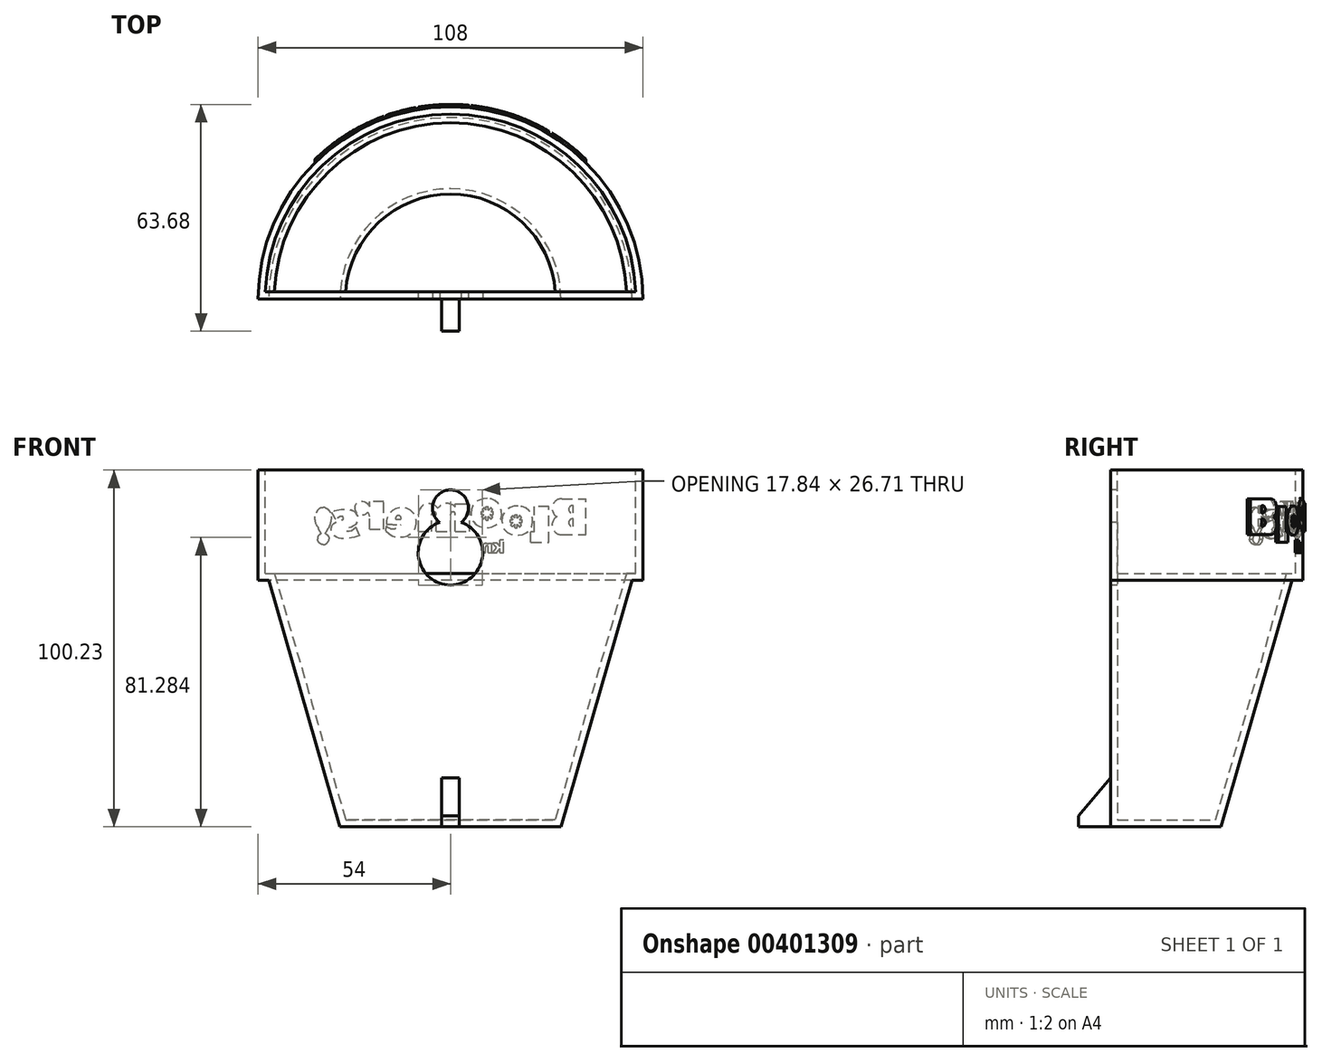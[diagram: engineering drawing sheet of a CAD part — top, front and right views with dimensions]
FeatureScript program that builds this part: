
annotation { "Feature Type Name" : "Feature", "Feature Type Description" : "" }
export const myFeature = defineFeature(function(context is Context, id is Id, definition is map)
    precondition{}
    {
        {
            var Q0;
            Q0=qCreatedBy(makeId("Front.planeOp"),FACE);
            var sketch = newSketch(context, id + "F0", { "sketchPlane" : qUnion([Q0])});
            skLineSegment(sketch, "E0", {"start": v(0, 49.42) * mm, "end": v(-54, 49.42) * mm});
            skLineSegment(sketch, "E1", {"start": v(-54, 49.42) * mm, "end": v(-54, 18.42) * mm});
            skLineSegment(sketch, "E2", {"start": v(0, -50.8) * mm, "end": v(-31, -50.8) * mm});
            skLineSegment(sketch, "E3", {"start": v(-54, 18.42) * mm, "end": v(-51, 18.42) * mm});
            skLineSegment(sketch, "E4", {"start": v(0, 49.42) * mm, "end": v(0, -50.8) * mm});
            skLineSegment(sketch, "E5", {"start": v(-51, 18.42) * mm, "end": v(-31, -50.8) * mm});
            skLineSegment(sketch, "E6.MirrorCS", {"start": v(0, 49.42) * mm, "end": v(54, 49.42) * mm});
            skLineSegment(sketch, "E7.MirrorCS", {"start": v(54, 49.42) * mm, "end": v(54, 18.42) * mm});
            skLineSegment(sketch, "E8.MirrorCS", {"start": v(54, 18.42) * mm, "end": v(51, 18.42) * mm});
            skLineSegment(sketch, "E9.MirrorCS", {"start": v(51, 18.42) * mm, "end": v(31, -50.8) * mm});
            skLineSegment(sketch, "E10.MirrorCS", {"start": v(0, -50.8) * mm, "end": v(31, -50.8) * mm});
            skSolve(sketch);
        }
        {
            var Q0;
            {var subQ0=sQuery(id+"F0.wireOp",EDGE,"E3");Q0=makeQuery(id+"F0.imprint","IMPRINT",FACE,{"disambiguationData":[TD([[makeQuery(id+"F0.imprint","IMPRINT",EDGE,{"derivedFrom":subQ0}),1.0]])]});}
            var Q1;
            {var subQ1=sQuery(id+"F0.wireOp",EDGE,"E0");Q1=makeQuery(id+"F0.imprint","IMPRINT",FACE,{"disambiguationData":[TD([[makeQuery(id+"F0.imprint","IMPRINT",EDGE,{"derivedFrom":subQ1}),1.0]])]});}
            var Q2;
            Q2=makeQuery(id+"F0.imprint","IMPRINT",FACE,{"disambiguationData":[TD([[makeQuery(id+"F0.imprint","IMPRINT",EDGE,{"derivedFrom":sQuery(id+"F0.wireOp",EDGE,"Kfnrekvc-ZjTY-c2iQ-cK4z-hKnBe4uEAVNk")}),1.0]])]});
            var Q3;
            Q3=sQuery(id+"F0.wireOp",EDGE,"E4");
            revolve(context, id + "F1", {"entities" : qUnion([Q0, Q1, Q2]), "axis" : qUnion([Q3]), "revolveType" : RevolveType.ONE_DIRECTION, "angle" : 180 * degree});
        }
        {
            var Q0;
            Q0=makeQuery(id+"FK2OT3XlAi37Aaq_1.splitOp","SPLIT",FACE,{"derivedFrom":makeQuery(id+"F1.opRevolve","SWEPT_FACE",FACE,{"disambiguationData":[OSD([sQuery(id+"F0.wireOp",EDGE,"E0")])]}),"isFromBackBody":true});
            shell(context, id + "F2", {"entities" : qUnion([Q0]), "thickness" : 2 * mm});
        }
        {
            var Q0;
            Q0=qCreatedBy(makeId("Front.planeOp"),FACE);
            var sketch = newSketch(context, id + "F3", { "sketchPlane" : qUnion([Q0])});
            skLineSegment(sketch, "E11.bottom", {"start": v(-2.5, -35.8) * mm, "end": v(2.5, -35.8) * mm});
            skLineSegment(sketch, "E11.top", {"start": v(-2.5, -50.8) * mm, "end": v(2.5, -50.8) * mm});
            skLineSegment(sketch, "E11.left", {"start": v(-2.5, -35.8) * mm, "end": v(-2.5, -50.8) * mm});
            skLineSegment(sketch, "E11.right", {"start": v(2.5, -35.8) * mm, "end": v(2.5, -50.8) * mm});
            skPoint(sketch, "E11.middle", {"position": v(0, -43.3) * mm});
            skSolve(sketch);
        }
        {
            var Q0;
            Q0=qSketchRegion(id+"F3",true);
            extrude(context, id + "F4", {"entities" : qUnion([Q0]), "operationType" : NewBodyOperationType.ADD, "depth" : 9 * mm});
        }
        {
            var Q0;
            Q0=qCreatedBy(makeId("Front.planeOp"),FACE);
            var sketch = newSketch(context, id + "F5", { "sketchPlane" : qUnion([Q0])});
            skCircle(sketch, "E12", {"center": v(0, 38.78) * mm, "radius": 5.05 * mm});
            skCircle(sketch, "E13", {"center": v(0, 26.17) * mm, "radius": 9.05 * mm});
            skSolve(sketch);
        }
        {
            var Q0;
            {var subQ0=sQuery(id+"F5.wireOp",EDGE,"E13");var subQ1=sQuery(id+"F5.wireOp",EDGE,"E12");var subQ2=makeQuery(id+"F5.imprint","INTERSECT",VERTEX,{"disambiguationData":[OD(0.0)],"derivedFrom":[subQ1,subQ0]});Q0=makeQuery(id+"F5.imprint","IMPRINT",FACE,{"disambiguationData":[TD([[makeQuery(id+"F5.imprint","IMPRINT",EDGE,{"disambiguationData":[TD([[subQ2,1.0]])],"derivedFrom":subQ1}),1.0]])]});}
            var Q1;
            {var subQ0=sQuery(id+"F5.wireOp",EDGE,"E13");var subQ1=sQuery(id+"F5.wireOp",EDGE,"E12");var subQ2=makeQuery(id+"F5.imprint","INTERSECT",VERTEX,{"disambiguationData":[OD(0.0)],"derivedFrom":[subQ1,subQ0]});Q1=makeQuery(id+"F5.imprint","IMPRINT",FACE,{"disambiguationData":[TD([[makeQuery(id+"F5.imprint","IMPRINT",EDGE,{"disambiguationData":[TD([[subQ2,-1.0]])],"derivedFrom":subQ1}),-1.0]])]});}
            var Q2;
            {var subQ0=sQuery(id+"F5.wireOp",EDGE,"E13");var subQ1=sQuery(id+"F5.wireOp",EDGE,"E12");var subQ2=makeQuery(id+"F5.imprint","INTERSECT",VERTEX,{"disambiguationData":[OD(0.0)],"derivedFrom":[subQ1,subQ0]});Q2=makeQuery(id+"F5.imprint","IMPRINT",FACE,{"disambiguationData":[TD([[makeQuery(id+"F5.imprint","IMPRINT",EDGE,{"disambiguationData":[TD([[subQ2,-1.0]])],"derivedFrom":subQ1}),1.0]])]});}
            var Q3;
            Q3=sQuery(id+"F5.wireOp",EDGE,"E12");
            var Q4;
            Q4=sQuery(id+"F5.wireOp",EDGE,"E13");
            extrude(context, id + "F6", {"entities" : qUnion([Q0, Q1, Q2]), "operationType" : NewBodyOperationType.REMOVE, "surfaceEntities" : qUnion([Q3, Q4]), "oppositeDirection" : true, "depth" : 10 * mm});
        }
        {
            var Q0;
            Q0=makeQuery(id+"F4.opExtrude","CAP_EDGE",EDGE,{"disambiguationData":[OSD([sQuery(id+"F3.wireOp",EDGE,"E11.bottom")])],"isStart":false});
            chamfer(context, id + "F7", {"entities" : qUnion([Q0]), "chamferType" : ChamferType.OFFSET_ANGLE, "width" : 10 * mm, "oppositeDirection" : false, "angle" : 50 * degree, "tangentPropagation" : true});
        }
        {
            var Q0;
            Q0=makeQuery(id+"F2.opShell","OFFSET_FACE",FACE,{"disambiguationData":[OSD([sQuery(id+"F0.wireOp",EDGE,"E0"),sQuery(id+"F0.wireOp",EDGE,"E1"),sQuery(id+"F0.wireOp",EDGE,"E2"),sQuery(id+"F0.wireOp",EDGE,"E3"),sQuery(id+"F0.wireOp",EDGE,"E4"),sQuery(id+"F0.wireOp",EDGE,"E5")])]});
            cPlane(context, id + "F8", {"entities" : qUnion([Q0]), "cplaneType" : CPlaneType.OFFSET, "offset" : 52.7 * mm, "width" : 150 * mm, "height" : 150 * mm});
        }
        {
            var Q0;
            Q0=qCreatedBy(id+"F8.planeOp",FACE);
            var sketch = newSketch(context, id + "F9", { "sketchPlane" : qUnion([Q0])});
            skLineSegment(sketch, "E14", {"start": v(-37.98, 41.35) * mm, "end": v(-37.98, 31.23) * mm});
            skLineSegment(sketch, "E15", {"start": v(-37.98, 31.23) * mm, "end": v(-31.26, 31.23) * mm});
            skLineSegment(sketch, "E16", {"start": v(-37.98, 41.35) * mm, "end": v(-31.26, 41.35) * mm});
            skArc(sketch, "E17", {"start": v(-29.86, 36.3) * mm, "mid": v(-28.64, 39.36) * mm, "end": v(-31.26, 41.35) * mm});
            skArc(sketch, "E18", {"start": v(-31.26, 31.23) * mm, "mid": v(-28.62, 33.24) * mm, "end": v(-29.86, 36.3) * mm});
            skLineSegment(sketch, "E19", {"start": v(-34.46, 39.42) * mm, "end": v(-34.46, 37.35) * mm});
            skArc(sketch, "E20", {"start": v(-34.46, 37.35) * mm, "mid": v(-33.23, 38.38) * mm, "end": v(-34.46, 39.42) * mm});
            skArc(sketch, "E21", {"start": v(-34.46, 33.62) * mm, "mid": v(-33.23, 34.66) * mm, "end": v(-34.46, 35.69) * mm});
            skLineSegment(sketch, "E22.trimOffspring", {"start": v(-34.46, 35.69) * mm, "end": v(-34.46, 33.62) * mm});
            skLineSegment(sketch, "E23", {"start": v(-27.67, 39.2) * mm, "end": v(-27.67, 29.07) * mm});
            skLineSegment(sketch, "E24", {"start": v(-27.67, 29.07) * mm, "end": v(-22.58, 29.07) * mm});
            skLineSegment(sketch, "E25", {"start": v(-22.58, 29.07) * mm, "end": v(-22.58, 32.1) * mm});
            skLineSegment(sketch, "E26", {"start": v(-22.58, 32.1) * mm, "end": v(-23.6, 32.1) * mm});
            skLineSegment(sketch, "E27", {"start": v(-23.6, 32.1) * mm, "end": v(-23.6, 39.2) * mm});
            skLineSegment(sketch, "E28", {"start": v(-23.6, 39.2) * mm, "end": v(-27.67, 39.2) * mm});
            skFitSpline(sketch, "E29", {"points": [v(-18.97, 39.3) * mm, v(-20.87, 38.92) * mm, v(-22.46, 37.44) * mm, v(-22.99, 35.82) * mm, v(-22.97, 34.09) * mm, v(-22.03, 32.34) * mm, v(-20.21, 31.27) * mm, v(-18.57, 31.14) * mm, v(-16.6, 31.5) * mm, v(-14.9, 33.15) * mm, v(-14.42, 35.37) * mm, v(-14.96, 37.3) * mm, v(-16.45, 38.75) * mm, v(-18.2, 39.28) * mm, v(-18.97, 39.3) * mm]});
            skLineSegment(sketch, "E30.bottom", {"start": v(-18.74, 36.9) * mm, "end": v(-18.06, 36.9) * mm});
            skLineSegment(sketch, "E30.top", {"start": v(-18.74, 33.18) * mm, "end": v(-18.06, 33.18) * mm});
            skLineSegment(sketch, "E30.left", {"start": v(-18.74, 36.9) * mm, "end": v(-18.74, 35.88) * mm});
            skLineSegment(sketch, "E30.right", {"start": v(-18.06, 36.9) * mm, "end": v(-18.06, 35.97) * mm});
            skLineSegment(sketch, "E31.bottom", {"start": v(-20.12, 35.52) * mm, "end": v(-19.41, 35.52) * mm});
            skLineSegment(sketch, "E31.top", {"start": v(-20.12, 34.7) * mm, "end": v(-19.25, 34.7) * mm});
            skLineSegment(sketch, "E31.left", {"start": v(-20.12, 35.52) * mm, "end": v(-20.12, 34.7) * mm});
            skLineSegment(sketch, "E31.right", {"start": v(-16.76, 35.52) * mm, "end": v(-16.76, 34.7) * mm});
            skLineSegment(sketch, "E32", {"start": v(-19.97, 36.08) * mm, "end": v(-19.41, 35.52) * mm});
            skLineSegment(sketch, "E33", {"start": v(-17.4, 33.5) * mm, "end": v(-16.88, 34.02) * mm});
            skLineSegment(sketch, "E34", {"start": v(-19.45, 36.58) * mm, "end": v(-19.97, 36.08) * mm});
            skLineSegment(sketch, "E35", {"start": v(-19.97, 33.94) * mm, "end": v(-19.45, 33.42) * mm});
            skLineSegment(sketch, "E36", {"start": v(-19.45, 33.42) * mm, "end": v(-18.74, 34.17) * mm});
            skLineSegment(sketch, "E37", {"start": v(-16.94, 36.08) * mm, "end": v(-17.48, 36.58) * mm});
            skLineSegment(sketch, "E38", {"start": v(-17.48, 36.58) * mm, "end": v(-18.06, 35.97) * mm});
            skLineSegment(sketch, "E39.trimOffspring", {"start": v(-18.74, 35.88) * mm, "end": v(-19.45, 36.58) * mm});
            skLineSegment(sketch, "E40.trimOffspring", {"start": v(-19.25, 34.7) * mm, "end": v(-19.97, 33.94) * mm});
            skLineSegment(sketch, "E41.trimOffspring", {"start": v(-18.06, 34.17) * mm, "end": v(-17.4, 33.5) * mm});
            skLineSegment(sketch, "E42.trimOffspring", {"start": v(-18.74, 34.17) * mm, "end": v(-18.74, 33.18) * mm});
            skLineSegment(sketch, "E43.trimOffspring", {"start": v(-18.06, 34.17) * mm, "end": v(-18.06, 33.18) * mm});
            skLineSegment(sketch, "E44.trimOffspring", {"start": v(-17.47, 35.52) * mm, "end": v(-16.94, 36.08) * mm});
            skLineSegment(sketch, "E45.trimOffspring", {"start": v(-17.47, 35.52) * mm, "end": v(-16.76, 35.52) * mm});
            skLineSegment(sketch, "E46.trimOffspring", {"start": v(-17.56, 34.7) * mm, "end": v(-16.76, 34.7) * mm});
            skFitSpline(sketch, "E47", {"points": [v(-10.3, 41.42) * mm, v(-12.2, 41.04) * mm, v(-13.79, 39.56) * mm, v(-14.32, 37.94) * mm, v(-14.3, 36.2) * mm, v(-13.36, 34.46) * mm, v(-11.55, 33.39) * mm, v(-9.9, 33.26) * mm, v(-7.94, 33.62) * mm, v(-6.23, 35.27) * mm, v(-5.76, 37.49) * mm, v(-6.3, 39.41) * mm, v(-7.79, 40.86) * mm, v(-9.54, 41.4) * mm, v(-10.3, 41.42) * mm]});
            skLineSegment(sketch, "E48", {"start": v(-17.56, 34.7) * mm, "end": v(-16.88, 34.02) * mm});
            skLineSegment(sketch, "E49", {"start": v(-5.38, 32.17) * mm, "end": v(-5.38, 39.97) * mm});
            skLineSegment(sketch, "E50", {"start": v(-5.38, 39.97) * mm, "end": v(-1.39, 39.97) * mm});
            skLineSegment(sketch, "E51", {"start": v(-1.39, 39.97) * mm, "end": v(-1.39, 39) * mm});
            skLineSegment(sketch, "E52", {"start": v(-5.38, 32.17) * mm, "end": v(-1.38, 32.17) * mm});
            skLineSegment(sketch, "E53", {"start": v(-1.38, 32.17) * mm, "end": v(-1.38, 36.98) * mm});
            skLineSegment(sketch, "E54", {"start": v(0, 36.98) * mm, "end": v(0, 32.17) * mm});
            skLineSegment(sketch, "E55", {"start": v(0, 32.17) * mm, "end": v(3.95, 32.17) * mm});
            skLineSegment(sketch, "E56", {"start": v(3.95, 32.17) * mm, "end": v(3.95, 36.98) * mm});
            skLineSegment(sketch, "E57", {"start": v(5.25, 36.98) * mm, "end": v(5.25, 32.17) * mm});
            skLineSegment(sketch, "E58", {"start": v(5.25, 32.17) * mm, "end": v(9.02, 32.17) * mm});
            skLineSegment(sketch, "E59", {"start": v(9.02, 32.17) * mm, "end": v(9.02, 36.98) * mm});
            skArc(sketch, "E60", {"start": v(5.25, 36.98) * mm, "mid": v(4.6, 37.63) * mm, "end": v(3.95, 36.98) * mm});
            skArc(sketch, "E61", {"start": v(0, 36.98) * mm, "mid": v(-0.69, 37.67) * mm, "end": v(-1.38, 36.98) * mm});
            skArc(sketch, "E62", {"start": v(3.53, 38.66) * mm, "mid": v(1.15, 40.01) * mm, "end": v(-1.39, 39) * mm});
            skArc(sketch, "E63", {"start": v(9.02, 36.98) * mm, "mid": v(6.9, 39.85) * mm, "end": v(3.53, 38.66) * mm});
            skArc(sketch, "E64", {"start": v(13.95, 34.1) * mm, "mid": v(15.9, 32.9) * mm, "end": v(18.03, 33.72) * mm});
            skLineSegment(sketch, "E65", {"start": v(13.95, 34.1) * mm, "end": v(18.03, 34.17) * mm});
            skLineSegment(sketch, "E66", {"start": v(13.9, 35.57) * mm, "end": v(15.36, 35.6) * mm});
            skArc(sketch, "E67", {"start": v(15.36, 35.6) * mm, "mid": v(14.6, 36.63) * mm, "end": v(13.9, 35.57) * mm});
            skLineSegment(sketch, "E68", {"start": v(18.03, 33.72) * mm, "end": v(18.06, 32.3) * mm});
            skLineSegment(sketch, "E69", {"start": v(22.7, 39.16) * mm, "end": v(22.7, 40.55) * mm});
            skLineSegment(sketch, "E70", {"start": v(22.7, 40.55) * mm, "end": v(18.72, 40.58) * mm});
            skLineSegment(sketch, "E71", {"start": v(18.72, 40.58) * mm, "end": v(18.72, 32.74) * mm});
            skLineSegment(sketch, "E72", {"start": v(18.72, 32.74) * mm, "end": v(22.7, 32.74) * mm});
            skLineSegment(sketch, "E73", {"start": v(22.7, 32.74) * mm, "end": v(22.7, 36.3) * mm});
            skLineSegment(sketch, "E74", {"start": v(33.3, 37.45) * mm, "end": v(32.27, 35.62) * mm});
            skFitSpline(sketch, "E75", {"points": [v(33.3, 37.45) * mm, v(32.36, 37.96) * mm, v(31.25, 38.2) * mm, v(30.16, 38.3) * mm, v(28.65, 38.26) * mm, v(27.14, 37.83) * mm, v(26.29, 37.06) * mm, v(25.86, 36.05) * mm, v(26.07, 34.84) * mm, v(26.79, 33.99) * mm, v(28.33, 33.35) * mm, v(29.12, 33.1) * mm, v(29.36, 32.85) * mm, v(29.3, 32.47) * mm, v(29, 32.12) * mm, v(28.48, 32.1) * mm, v(27.57, 32.38) * mm, v(26.88, 32.96) * mm, v(26.6, 33.22) * mm, v(26.49, 33.3) * mm], "startDerivative": vector(-15.65, 9.87) * mm, "endDerivative": vector(-4.84, 3.4) * mm});
            skFitSpline(sketch, "E76", {"points": [v(32.27, 35.62) * mm, v(31.94, 35.79) * mm, v(31.56, 36.06) * mm, v(31.13, 36.28) * mm, v(30.73, 36.4) * mm, v(30.1, 36.28) * mm, v(29.89, 35.88) * mm, v(30.08, 35.62) * mm, v(30.64, 35.32) * mm, v(31.42, 35.1) * mm, v(32.1, 34.87) * mm, v(32.63, 34.52) * mm, v(33.07, 34.09) * mm, v(33.37, 33.46) * mm, v(33.46, 33) * mm, v(33.46, 32.48) * mm, v(33.31, 31.72) * mm, v(32.8, 31.07) * mm, v(32.27, 30.71) * mm, v(31.46, 30.26) * mm, v(30.44, 30.1) * mm, v(29.25, 30.17) * mm, v(28.56, 30.21) * mm, v(27.53, 30.4) * mm, v(26.65, 30.67) * mm, v(26.13, 30.83) * mm, v(25.52, 31) * mm, v(24, 31.52) * mm], "startDerivative": vector(-12.22, 5.14) * mm, "endDerivative": vector(-29.8, 10.92) * mm});
            skLineSegment(sketch, "E77", {"start": v(26.49, 33.3) * mm, "end": v(25.52, 31) * mm});
            skFitSpline(sketch, "E78", {"points": [v(35.16, 31.53) * mm, v(34.54, 32.68) * mm, v(33.94, 33.8) * mm, v(33.6, 34.86) * mm, v(33.49, 36.06) * mm, v(33.7, 37.34) * mm, v(34.45, 38.46) * mm, v(35.3, 38.86) * mm, v(36.02, 38.89) * mm, v(36.86, 38.44) * mm, v(37.6, 37.54) * mm, v(38.02, 36.55) * mm, v(37.98, 35.4) * mm, v(37.68, 34.14) * mm, v(37.17, 33.21) * mm, v(36.7, 32.27) * mm, v(36.3, 31.56) * mm, v(36.34, 31.34) * mm], "startDerivative": vector(-9.25, 17.51) * mm, "endDerivative": vector(7.08, -5.7) * mm});
            skFitSpline(sketch, "E79", {"points": [v(35.16, 31.53) * mm, v(34.67, 31.23) * mm, v(34.3, 30.83) * mm, v(34.1, 30) * mm, v(34.28, 29.4) * mm, v(34.62, 28.94) * mm, v(35.02, 28.64) * mm, v(35.5, 28.5) * mm, v(36.33, 28.63) * mm, v(37.12, 29.37) * mm, v(37.32, 30.35) * mm, v(37.03, 31) * mm, v(36.66, 31.33) * mm, v(36.3, 31.56) * mm], "startDerivative": vector(-7.2, -4.04) * mm, "endDerivative": vector(-5.92, 3.66) * mm});
            skFitSpline(sketch, "E80", {"points": [v(22.7, 39.16) * mm, v(23.03, 39.64) * mm, v(23.42, 40.06) * mm, v(23.73, 40.35) * mm, v(24.26, 40.57) * mm, v(24.84, 40.64) * mm, v(25.53, 40.57) * mm, v(26.1, 40.3) * mm, v(26.54, 39.8) * mm, v(26.74, 39.36) * mm, v(26.8, 38.85) * mm, v(26.68, 38.15) * mm, v(26.4, 37.56) * mm, v(25.92, 37.08) * mm, v(25.1, 36.8) * mm, v(24.42, 36.74) * mm, v(23.86, 36.98) * mm, v(23.58, 37.28) * mm, v(23.43, 37.42) * mm, v(23.23, 37.46) * mm, v(23.04, 37.32) * mm, v(22.94, 37.12) * mm, v(22.7, 36.3) * mm, v(23.06, 35.75) * mm], "startDerivative": vector(6.72, 10.93) * mm, "endDerivative": vector(10.8, -11.25) * mm});
            skLineSegment(sketch, "E81", {"start": v(35.7, 38.92) * mm, "end": v(35.7, 28.5) * mm, "construction": true});
            skFitSpline(sketch, "E82.MirrorCS", {"points": [v(36.25, 31.53) * mm, v(36.88, 32.68) * mm, v(37.48, 33.8) * mm, v(37.82, 34.86) * mm, v(37.93, 36.06) * mm, v(37.71, 37.34) * mm, v(36.97, 38.46) * mm, v(36.12, 38.86) * mm, v(35.4, 38.89) * mm, v(34.56, 38.44) * mm, v(33.81, 37.54) * mm, v(33.4, 36.55) * mm, v(33.44, 35.4) * mm, v(33.74, 34.14) * mm, v(34.25, 33.21) * mm, v(34.7, 32.27) * mm, v(35.12, 31.56) * mm, v(35.08, 31.34) * mm], "startDerivative": vector(9.25, 17.51) * mm, "endDerivative": vector(-7.08, -5.7) * mm});
            skFitSpline(sketch, "E83.MirrorCS", {"points": [v(36.25, 31.53) * mm, v(36.75, 31.23) * mm, v(37.12, 30.83) * mm, v(37.32, 30) * mm, v(37.14, 29.4) * mm, v(36.8, 28.94) * mm, v(36.4, 28.64) * mm, v(35.92, 28.5) * mm, v(35.1, 28.63) * mm, v(34.3, 29.37) * mm, v(34.1, 30.35) * mm, v(34.4, 31) * mm, v(34.76, 31.33) * mm, v(35.12, 31.56) * mm], "startDerivative": vector(7.2, -4.04) * mm, "endDerivative": vector(5.92, 3.66) * mm});
            skPoint(sketch, "E84.center.orphan", {"position": v(13.9, 34.67) * mm});
            skFitSpline(sketch, "E85", {"points": [v(18.03, 34.17) * mm, v(18.03, 34.7) * mm, v(17.92, 35.49) * mm, v(17.61, 36.55) * mm, v(17.02, 37.44) * mm, v(16.13, 38.19) * mm, v(14.97, 38.7) * mm, v(14.1, 38.85) * mm, v(12.84, 38.8) * mm, v(11.17, 38.09) * mm, v(10.23, 37.08) * mm, v(9.76, 36.06) * mm, v(9.6, 35.11) * mm, v(9.7, 33.68) * mm, v(10.2, 32.57) * mm, v(10.95, 31.71) * mm, v(11.75, 31.16) * mm, v(12.56, 30.78) * mm, v(13.37, 30.62) * mm, v(14.26, 30.56) * mm, v(15.2, 30.6) * mm, v(16.3, 30.93) * mm, v(17.16, 31.48) * mm, v(17.72, 31.95) * mm, v(18.16, 32.4) * mm], "startDerivative": vector(0.59, 17.06) * mm, "endDerivative": vector(10.98, 9.93) * mm});
            skLineSegment(sketch, "E86.bottom", {"start": v(-10.64, 39.1) * mm, "end": v(-9.96, 39.1) * mm});
            skLineSegment(sketch, "E86.top", {"start": v(-10.64, 35.38) * mm, "end": v(-9.96, 35.38) * mm});
            skLineSegment(sketch, "E86.left", {"start": v(-10.64, 39.1) * mm, "end": v(-10.64, 38.08) * mm});
            skLineSegment(sketch, "E86.right", {"start": v(-9.96, 39.1) * mm, "end": v(-9.96, 38.17) * mm});
            skLineSegment(sketch, "E87.bottom", {"start": v(-12.02, 37.72) * mm, "end": v(-11.31, 37.72) * mm});
            skLineSegment(sketch, "E87.top", {"start": v(-12.02, 36.9) * mm, "end": v(-11.15, 36.9) * mm});
            skLineSegment(sketch, "E87.left", {"start": v(-12.02, 37.72) * mm, "end": v(-12.02, 36.9) * mm});
            skLineSegment(sketch, "E87.right", {"start": v(-8.66, 37.72) * mm, "end": v(-8.66, 36.9) * mm});
            skLineSegment(sketch, "E88", {"start": v(-11.87, 38.28) * mm, "end": v(-11.31, 37.72) * mm});
            skLineSegment(sketch, "E89", {"start": v(-9.3, 35.7) * mm, "end": v(-8.78, 36.22) * mm});
            skLineSegment(sketch, "E90", {"start": v(-11.35, 38.78) * mm, "end": v(-11.87, 38.28) * mm});
            skLineSegment(sketch, "E91", {"start": v(-11.87, 36.14) * mm, "end": v(-11.35, 35.62) * mm});
            skLineSegment(sketch, "E92", {"start": v(-11.35, 35.62) * mm, "end": v(-10.64, 36.37) * mm});
            skLineSegment(sketch, "E93", {"start": v(-8.85, 38.28) * mm, "end": v(-9.38, 38.78) * mm});
            skLineSegment(sketch, "E94", {"start": v(-9.38, 38.78) * mm, "end": v(-9.96, 38.17) * mm});
            skLineSegment(sketch, "E95.trimOffspring", {"start": v(-10.64, 38.08) * mm, "end": v(-11.35, 38.78) * mm});
            skLineSegment(sketch, "E96.trimOffspring", {"start": v(-11.15, 36.9) * mm, "end": v(-11.87, 36.14) * mm});
            skLineSegment(sketch, "E97.trimOffspring", {"start": v(-9.96, 36.37) * mm, "end": v(-9.3, 35.7) * mm});
            skLineSegment(sketch, "E98.trimOffspring", {"start": v(-10.64, 36.37) * mm, "end": v(-10.64, 35.38) * mm});
            skLineSegment(sketch, "E99.trimOffspring", {"start": v(-9.96, 36.37) * mm, "end": v(-9.96, 35.38) * mm});
            skLineSegment(sketch, "E100.trimOffspring", {"start": v(-9.37, 37.72) * mm, "end": v(-8.85, 38.28) * mm});
            skLineSegment(sketch, "E101.trimOffspring", {"start": v(-9.37, 37.72) * mm, "end": v(-8.66, 37.72) * mm});
            skLineSegment(sketch, "E102.trimOffspring", {"start": v(-9.47, 36.9) * mm, "end": v(-8.66, 36.9) * mm});
            skLineSegment(sketch, "E103", {"start": v(-9.47, 36.9) * mm, "end": v(-8.78, 36.22) * mm});
            skLineSegment(sketch, "E104", {"start": v(-13.84, 29.78) * mm, "end": v(-14.95, 29.78) * mm});
            skLineSegment(sketch, "E105", {"start": v(-14.95, 26.24) * mm, "end": v(-13.84, 26.24) * mm});
            skLineSegment(sketch, "E106", {"start": v(-13.84, 26.24) * mm, "end": v(-13.84, 27.34) * mm});
            skLineSegment(sketch, "E107", {"start": v(-13.84, 27.34) * mm, "end": v(-12.98, 26.24) * mm});
            skLineSegment(sketch, "E108", {"start": v(-12.98, 26.24) * mm, "end": v(-11.8, 26.24) * mm});
            skLineSegment(sketch, "E109", {"start": v(-11.8, 26.24) * mm, "end": v(-12.88, 27.6) * mm});
            skLineSegment(sketch, "E110", {"start": v(-12.88, 27.6) * mm, "end": v(-11.87, 28.8) * mm});
            skLineSegment(sketch, "E111", {"start": v(-11.87, 28.8) * mm, "end": v(-13.17, 28.8) * mm});
            skLineSegment(sketch, "E112", {"start": v(-13.17, 28.8) * mm, "end": v(-13.84, 28) * mm});
            skLineSegment(sketch, "E113", {"start": v(-13.84, 28) * mm, "end": v(-13.84, 29.78) * mm});
            skLineSegment(sketch, "E114", {"start": v(-14.95, 29.78) * mm, "end": v(-14.95, 26.24) * mm});
            skLineSegment(sketch, "E115", {"start": v(-11.59, 26.24) * mm, "end": v(-10.6, 26.24) * mm});
            skLineSegment(sketch, "E116", {"start": v(-10.6, 26.24) * mm, "end": v(-10.6, 27.76) * mm});
            skLineSegment(sketch, "E117", {"start": v(-11.59, 26.24) * mm, "end": v(-11.59, 28.8) * mm});
            skLineSegment(sketch, "E118", {"start": v(-11.59, 28.8) * mm, "end": v(-10.6, 28.8) * mm});
            skLineSegment(sketch, "E119", {"start": v(-10.6, 28.8) * mm, "end": v(-10.6, 28.54) * mm});
            skLineSegment(sketch, "E120", {"start": v(-9.81, 26.24) * mm, "end": v(-8.9, 26.24) * mm});
            skLineSegment(sketch, "E121", {"start": v(-8.9, 26.24) * mm, "end": v(-8.9, 27.8) * mm});
            skLineSegment(sketch, "E122", {"start": v(-9.81, 26.24) * mm, "end": v(-9.81, 27.76) * mm});
            skArc(sketch, "E123", {"start": v(-9.81, 27.76) * mm, "mid": v(-10.2, 28.15) * mm, "end": v(-10.6, 27.76) * mm});
            skArc(sketch, "E124", {"start": v(-8.9, 27.8) * mm, "mid": v(-9.51, 28.73) * mm, "end": v(-10.6, 28.54) * mm});
            skSolve(sketch);
        }
        {
            var Q0;
            Q0 = qSketchRegion(id + "F9", true);
            extrude(context, id + "F10", {"entities" : qUnion([Q0]), "operationType" : NewBodyOperationType.ADD, "endBound" : BoundingType.UP_TO_NEXT, "oppositeDirection" : true, "depth" : 25 * mm});
        }
        {
            var Q0;
            Q0=makeQuery(id+"F1.opRevolve","SWEPT_FACE",FACE,{"disambiguationData":[OSD([sQuery(id+"F0.wireOp",EDGE,"E0")])]});
            var sketch = newSketch(context, id + "F11", { "sketchPlane" : qUnion([Q0])});
            skCircle(sketch, "E125", {"center": v(0, 0) * mm, "radius": 54.68 * mm});
            skCircle(sketch, "E126", {"center": v(0, 0) * mm, "radius": 73.66 * mm});
            skSolve(sketch);
        }
        {
            var Q0;
            Q0 = qSketchRegion(id + "F11", true);
            extrude(context, id + "F12", {"entities" : qUnion([Q0]), "operationType" : NewBodyOperationType.REMOVE, "oppositeDirection" : true, "depth" : 124 * mm});
        }
    });
